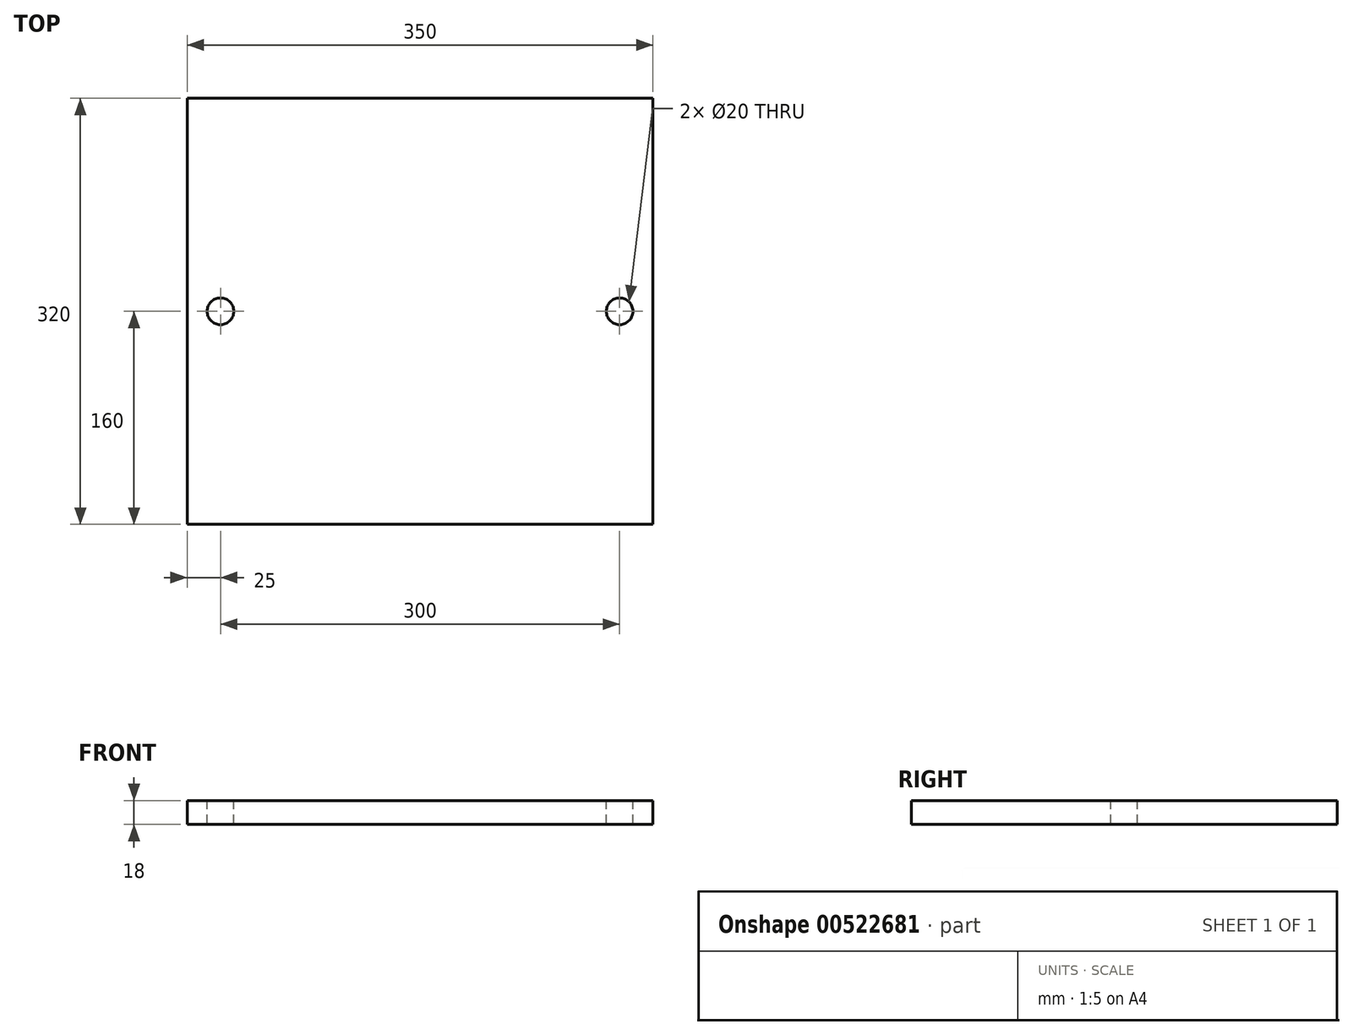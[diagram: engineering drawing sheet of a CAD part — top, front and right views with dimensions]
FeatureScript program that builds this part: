
annotation { "Feature Type Name" : "Feature", "Feature Type Description" : "" }
export const myFeature = defineFeature(function(context is Context, id is Id, definition is map)
    precondition{}
    {
        {
            var Q0;
            Q0=qCreatedBy(makeId("Top.planeOp"),FACE);
            var sketch = newSketch(context, id + "F0", { "sketchPlane" : qUnion([Q0])});
            skLineSegment(sketch, "E0.bottom", {"start": v(0, 0) * mm, "end": v(350, 0) * mm});
            skLineSegment(sketch, "E0.top", {"start": v(0, 320) * mm, "end": v(350, 320) * mm});
            skLineSegment(sketch, "E0.left", {"start": v(0, 0) * mm, "end": v(0, 320) * mm});
            skLineSegment(sketch, "E0.right", {"start": v(350, 0) * mm, "end": v(350, 320) * mm});
            skSolve(sketch);
        }
        {
            var Q0;
            Q0 = qSketchRegion(id + "F0", true);
            extrude(context, id + "F1", {"entities" : qUnion([Q0]), "depth" : 18 * mm, "offsetDistance" : 25 * mm});
        }
        {
            var Q0;
            Q0=makeQuery(id+"F1.opExtrude","CAP_FACE",FACE,{"disambiguationData":[OSD([sQuery(id+"F0.wireOp",EDGE,"E0.bottom"),sQuery(id+"F0.wireOp",EDGE,"E0.top"),sQuery(id+"F0.wireOp",EDGE,"E0.left"),sQuery(id+"F0.wireOp",EDGE,"E0.right")])],"isStart":false});
            var sketch = newSketch(context, id + "F2", { "sketchPlane" : qUnion([Q0])});
            skCircle(sketch, "E1", {"center": v(25, 160) * mm, "radius": 10 * mm});
            skCircle(sketch, "E2", {"center": v(325, 160) * mm, "radius": 10 * mm});
            skSolve(sketch);
        }
        {
            var Q0;
            Q0=makeQuery(id+"F2.imprint","IMPRINT",FACE,{"disambiguationData":[TD([[makeQuery(id+"F2.imprint","IMPRINT",EDGE,{"derivedFrom":sQuery(id+"F2.wireOp",EDGE,"E1")}),1.0]])]});
            var Q1;
            Q1=makeQuery(id+"F2.imprint","IMPRINT",FACE,{"disambiguationData":[TD([[makeQuery(id+"F2.imprint","IMPRINT",EDGE,{"derivedFrom":sQuery(id+"F2.wireOp",EDGE,"E2")}),1.0]])]});
            extrude(context, id + "F3", {"entities" : qUnion([Q0, Q1]), "operationType" : NewBodyOperationType.REMOVE, "endBound" : BoundingType.THROUGH_ALL, "oppositeDirection" : true, "depth" : 25 * mm, "offsetDistance" : 25 * mm});
        }
    });
